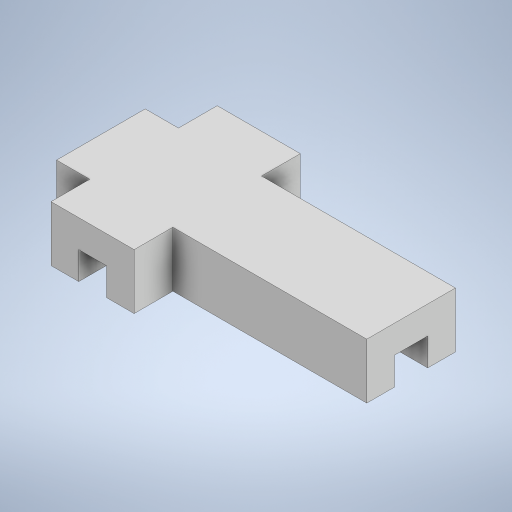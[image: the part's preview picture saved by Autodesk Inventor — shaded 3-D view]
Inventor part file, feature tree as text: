
AUTODESK INVENTOR PART (.ipt)
format: ipt  version: 2023 (Build 270158000, 158)  size: 335,872 bytes
history: native  units: mm
features: projected_geometry x8, sketch x5, extrude x4
ambient origin geometry x8: Origin, YZ Plane, XZ Plane, XY Plane, X Axis, Y Axis, Z Axis, Center Point
bodies: Solid1 (feature_tree)
feature tree (17):
  extrude  "Extrusion1"  Depth=6.0mm
  extrude  "Extrusion2"  Depth=12.0mm
  sketch  "Sketch3"  dims[d4=5.0mm d5=12.0mm]
  extrude  "Extrusion3"  Depth=12.0mm
  extrude  "Extrusion4"  Depth=5.0mm
  sketch  "Sketch1"  dims[d0=11.0mm d1=6.0mm]
  sketch  "Sketch2"  dims[d2=5.0mm d3=12.0mm]
  projected_geometry  "Projected Loop1"
  projected_geometry  "Projected Loop2"
  projected_geometry  "Projected Loop3"
  projected_geometry  "Projected Loop4"
  sketch  "Sketch4"  dims[d6=40.0mm d7=5.0mm]
  projected_geometry  "Projected Loop5"
  projected_geometry  "Projected Loop6"
  sketch  "Sketch5"  dims[d8=5.0mm d9=5.0mm d10=5.0mm d11=5.0mm d12=5.0mm d13=5.0mm d14=0.0mm d15=5.0mm d16=0.0mm d17=5.0mm d18=0.0mm d19=5.0mm d20=5.0mm d21=0.0mm]
  projected_geometry  "Projected Loop7"
  projected_geometry  "Projected Loop8"
